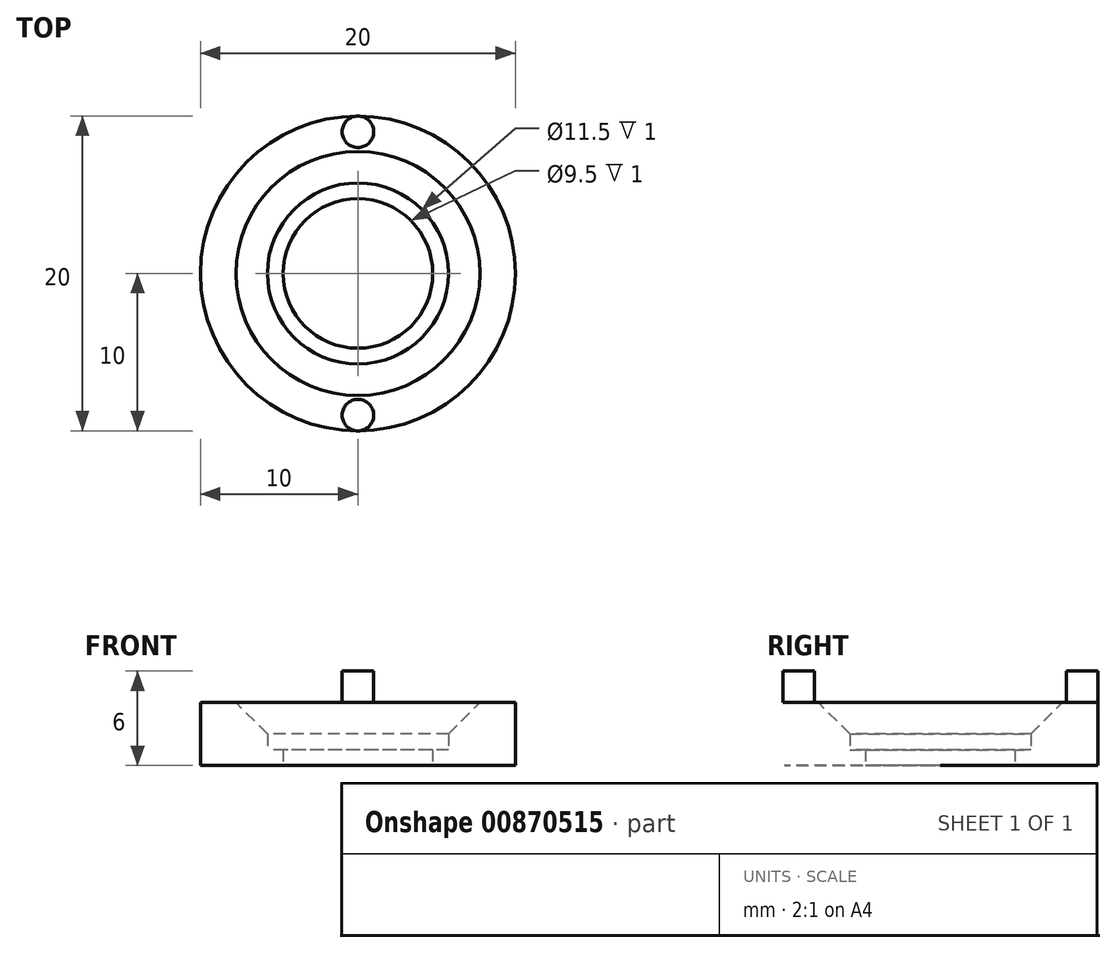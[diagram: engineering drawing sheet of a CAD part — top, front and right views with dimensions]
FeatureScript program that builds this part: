
annotation { "Feature Type Name" : "Feature", "Feature Type Description" : "" }
export const myFeature = defineFeature(function(context is Context, id is Id, definition is map)
    precondition{}
    {
        {
            var Q0;
            Q0=qCreatedBy(makeId("Top.planeOp"),FACE);
            var sketch = newSketch(context, id + "F0", { "sketchPlane" : qUnion([Q0])});
            skCircle(sketch, "E0", {"center": v(0, 0) * mm, "radius": 4.75 * mm});
            skCircle(sketch, "E1", {"center": v(0, 0) * mm, "radius": 10 * mm});
            skCircle(sketch, "E2", {"center": v(0, 0) * mm, "radius": 5.75 * mm});
            skLineSegment(sketch, "E3", {"start": v(-12.17, 0) * mm, "end": v(12.98, 0) * mm, "construction": true});
            skLineSegment(sketch, "E4", {"start": v(0, 13.57) * mm, "end": v(0, -14.95) * mm, "construction": true});
            skSolve(sketch);
        }
        {
            var Q0;
            Q0=makeQuery(id+"F0.imprint","IMPRINT",FACE,{"disambiguationData":[TD([[makeQuery(id+"F0.imprint","IMPRINT",EDGE,{"derivedFrom":sQuery(id+"F0.wireOp",EDGE,"E1")}),1.0]])]});
            var Q1;
            Q1=makeQuery(id+"F0.imprint","IMPRINT",FACE,{"disambiguationData":[TD([[makeQuery(id+"F0.imprint","IMPRINT",EDGE,{"derivedFrom":sQuery(id+"F0.wireOp",EDGE,"E2")}),-1.0]])]});
            var Q2;
            {var subQ0=sQuery(id+"F0.wireOp",EDGE,"2oGKKRCs-SF7h-0mtI-e1X6-1pv3B3WaliWI");var subQ1=sQuery(id+"F0.wireOp",EDGE,"E1");var subQ2=makeQuery(id+"F0.imprint","INTERSECT",VERTEX,{"disambiguationData":[OD(0.0)],"derivedFrom":[subQ1,subQ0]});Q2=makeQuery(id+"F0.imprint","IMPRINT",FACE,{"disambiguationData":[TD([[makeQuery(id+"F0.imprint","IMPRINT",EDGE,{"disambiguationData":[TD([[subQ2,1.0]])],"derivedFrom":subQ1}),1.0]])]});}
            var Q3;
            {var subQ0=sQuery(id+"F0.wireOp",EDGE,"5L21fKQo-Bj1C-wzZe-Lo9R-I6hjs5R9YJP7");var subQ1=sQuery(id+"F0.wireOp",EDGE,"E1");var subQ2=makeQuery(id+"F0.imprint","INTERSECT",VERTEX,{"disambiguationData":[OD(0.0)],"derivedFrom":[subQ1,subQ0]});Q3=makeQuery(id+"F0.imprint","IMPRINT",FACE,{"disambiguationData":[TD([[makeQuery(id+"F0.imprint","IMPRINT",EDGE,{"disambiguationData":[TD([[subQ2,-1.0]])],"derivedFrom":subQ1}),1.0]])]});}
            extrude(context, id + "F1", {"entities" : qUnion([Q0, Q1, Q2, Q3]), "depth" : 4 * mm, "offsetDistance" : 25 * mm});
        }
        {
            var Q0;
            Q0=makeQuery(id+"F0.imprint","IMPRINT",FACE,{"disambiguationData":[TD([[makeQuery(id+"F0.imprint","IMPRINT",EDGE,{"derivedFrom":sQuery(id+"F0.wireOp",EDGE,"E0")}),-1.0]])]});
            extrude(context, id + "F2", {"entities" : qUnion([Q0]), "operationType" : NewBodyOperationType.ADD, "depth" : 1 * mm, "offsetDistance" : 25 * mm});
        }
        {
            var Q0;
            Q0=makeQuery(id+"F1.opExtrude","CAP_EDGE",EDGE,{"disambiguationData":[OSD([sQuery(id+"F0.wireOp",EDGE,"E2")])],"isStart":false});
            chamfer(context, id + "F3", {"entities" : qUnion([Q0]), "width" : 2 * mm, "tangentPropagation" : true});
        }
        {
            var Q0;
            Q0=makeQuery(id+"F1.opExtrude","CAP_FACE",FACE,{"disambiguationData":[OSD([sQuery(id+"F0.wireOp",EDGE,"E1"),sQuery(id+"F0.wireOp",EDGE,"E2")])],"isStart":false});
            var sketch = newSketch(context, id + "F4", { "sketchPlane" : qUnion([Q0])});
            skLineSegment(sketch, "E5", {"start": v(0, 12.9) * mm, "end": v(0, -15.64) * mm, "construction": true});
            skCircle(sketch, "E6", {"center": v(0, 9) * mm, "radius": 1 * mm});
            skCircle(sketch, "E7", {"center": v(0, -9) * mm, "radius": 1 * mm});
            skSolve(sketch);
        }
        {
            var Q0;
            Q0=makeQuery(id+"F4.imprint","IMPRINT",FACE,{"disambiguationData":[TD([[makeQuery(id+"F4.imprint","IMPRINT",EDGE,{"derivedFrom":sQuery(id+"F4.wireOp",EDGE,"E6")}),1.0]])]});
            var Q1;
            Q1=makeQuery(id+"F4.imprint","IMPRINT",FACE,{"disambiguationData":[TD([[makeQuery(id+"F4.imprint","IMPRINT",EDGE,{"derivedFrom":sQuery(id+"F4.wireOp",EDGE,"E7")}),1.0]])]});
            extrude(context, id + "F5", {"entities" : qUnion([Q0, Q1]), "operationType" : NewBodyOperationType.ADD, "depth" : 2 * mm, "offsetDistance" : 25 * mm});
        }
    });
